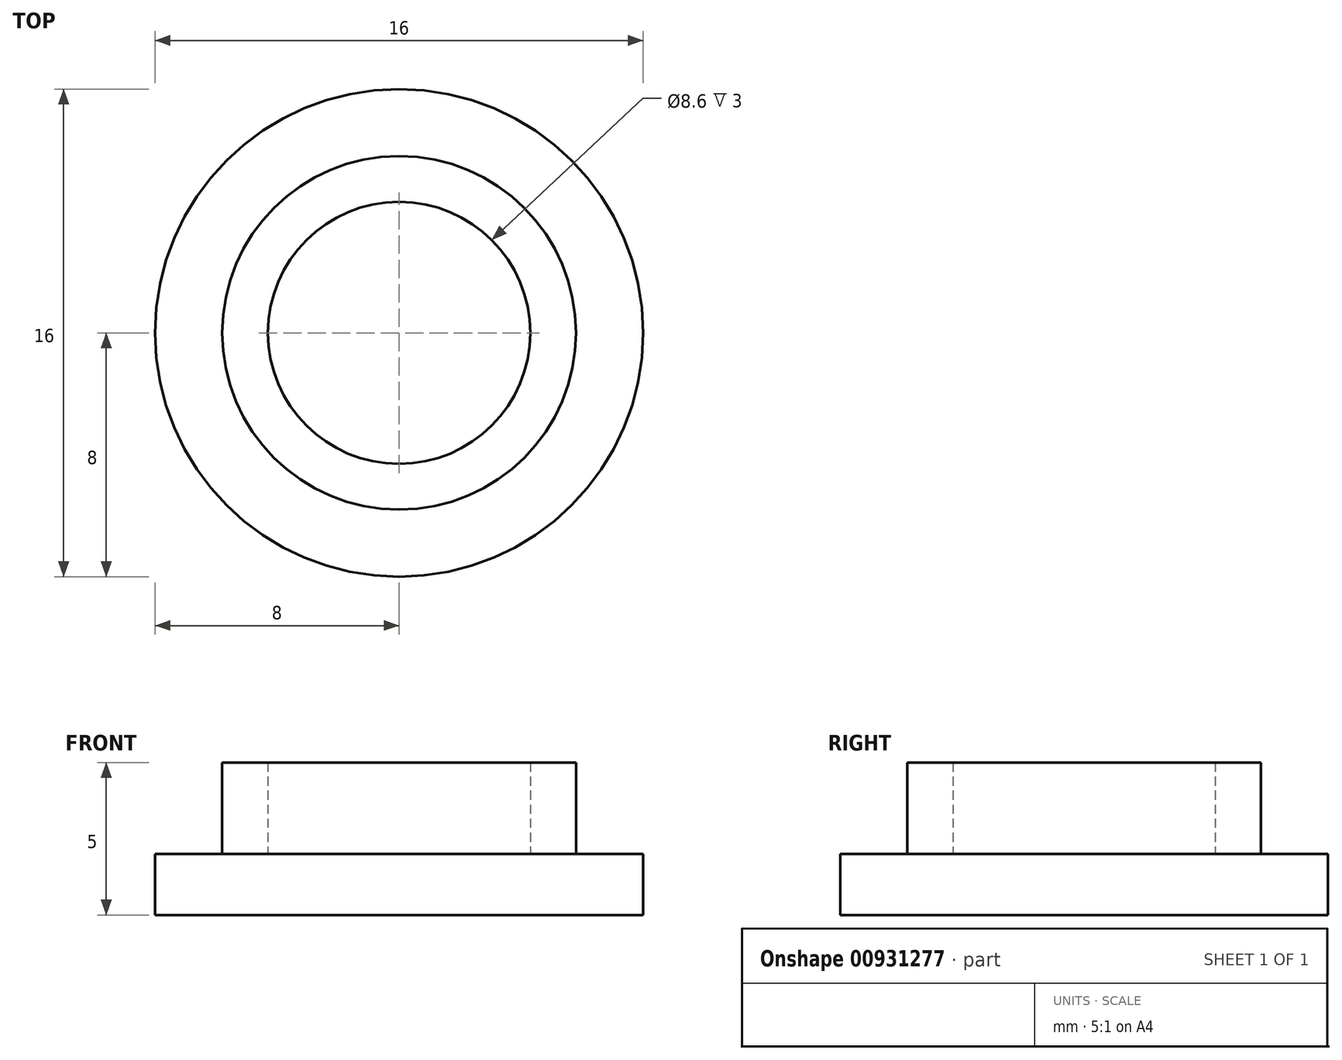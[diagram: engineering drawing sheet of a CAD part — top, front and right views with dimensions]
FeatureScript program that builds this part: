
annotation { "Feature Type Name" : "Feature", "Feature Type Description" : "" }
export const myFeature = defineFeature(function(context is Context, id is Id, definition is map)
    precondition{}
    {
        {
            var Q0;
            Q0=qCreatedBy(makeId("Top.planeOp"),FACE);
            var sketch = newSketch(context, id + "F0", { "sketchPlane" : qUnion([Q0])});
            skCircle(sketch, "E0", {"center": v(0, 0) * mm, "radius": 8 * mm});
            skCircle(sketch, "E1", {"center": v(0, 0) * mm, "radius": 4.3 * mm});
            skCircle(sketch, "E2", {"center": v(0, 0) * mm, "radius": 5.8 * mm});
            skSolve(sketch);
        }
        {
            var Q0;
            Q0=makeQuery(id+"F0.imprint","IMPRINT",FACE,{"disambiguationData":[TD([[makeQuery(id+"F0.imprint","IMPRINT",EDGE,{"derivedFrom":sQuery(id+"F0.wireOp",EDGE,"E1")}),-1.0]])]});
            extrude(context, id + "F1", {"entities" : qUnion([Q0]), "depth" : 3 * mm, "offsetDistance" : 25 * mm});
        }
        {
            var Q0;
            Q0=makeQuery(id+"F0.imprint","IMPRINT",FACE,{"disambiguationData":[TD([[makeQuery(id+"F0.imprint","IMPRINT",EDGE,{"derivedFrom":sQuery(id+"F0.wireOp",EDGE,"E0")}),1.0]])]});
            var Q1;
            Q1=makeQuery(id+"F0.imprint","IMPRINT",FACE,{"disambiguationData":[TD([[makeQuery(id+"F0.imprint","IMPRINT",EDGE,{"derivedFrom":sQuery(id+"F0.wireOp",EDGE,"E1")}),-1.0]])]});
            var Q2;
            Q2=makeQuery(id+"F0.imprint","IMPRINT",FACE,{"disambiguationData":[TD([[makeQuery(id+"F0.imprint","IMPRINT",EDGE,{"derivedFrom":sQuery(id+"F0.wireOp",EDGE,"E1")}),1.0]])]});
            extrude(context, id + "F2", {"entities" : qUnion([Q0, Q1, Q2]), "operationType" : NewBodyOperationType.ADD, "depth" : -2 * mm, "offsetDistance" : 25 * mm});
        }
    });
